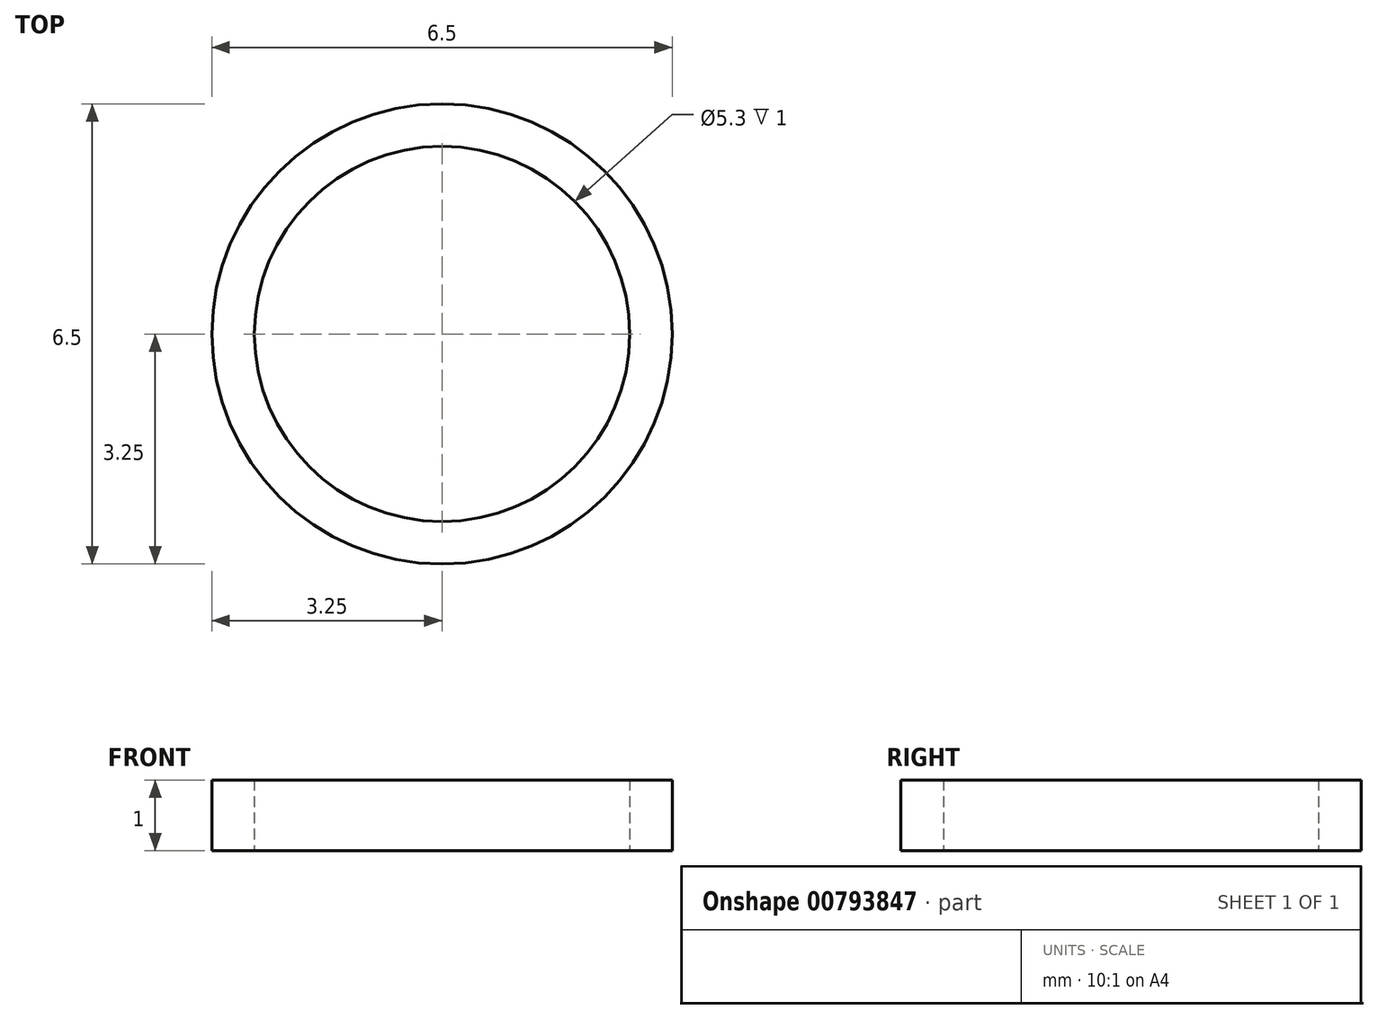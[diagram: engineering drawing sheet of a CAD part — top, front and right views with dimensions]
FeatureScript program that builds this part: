
annotation { "Feature Type Name" : "Feature", "Feature Type Description" : "" }
export const myFeature = defineFeature(function(context is Context, id is Id, definition is map)
    precondition{}
    {
        {
            var Q0;
            Q0=qCreatedBy(makeId("Top.planeOp"),FACE);
            var sketch = newSketch(context, id + "F0", { "sketchPlane" : qUnion([Q0])});
            skCircle(sketch, "E0", {"center": v(0, 0) * mm, "radius": 2.65 * mm});
            skCircle(sketch, "E1", {"center": v(0, 0) * mm, "radius": 3.25 * mm});
            skSolve(sketch);
        }
        {
            var Q0;
            Q0=qSketchRegion(id+"F0",true);
            extrude(context, id + "F1", {"entities" : qUnion([Q0]), "depth" : 1 * mm, "offsetDistance" : 25 * mm});
        }
    });
